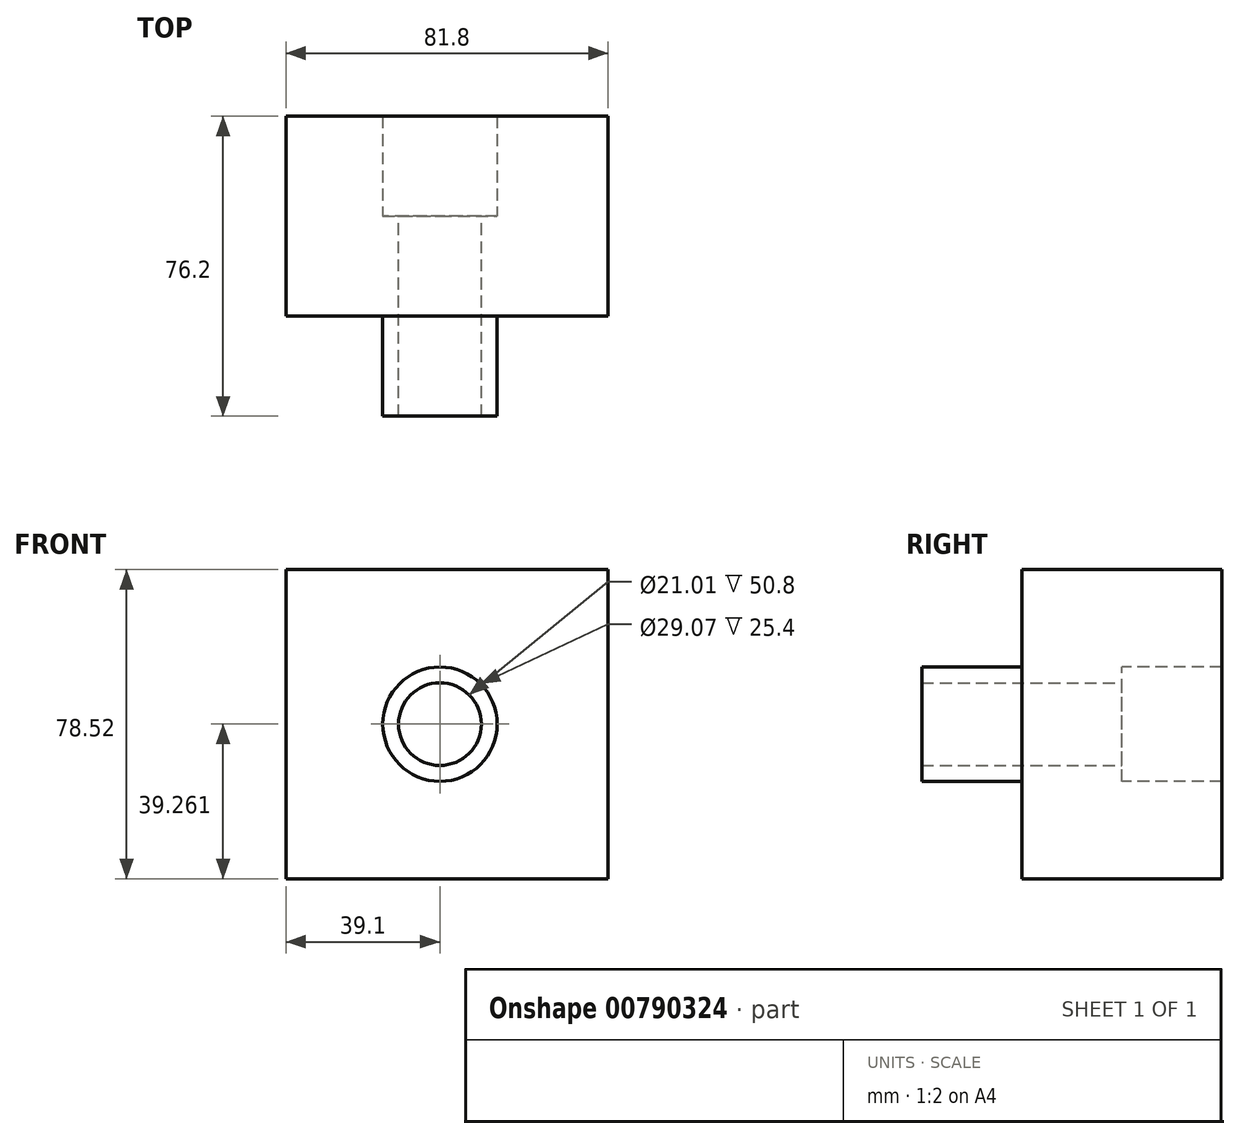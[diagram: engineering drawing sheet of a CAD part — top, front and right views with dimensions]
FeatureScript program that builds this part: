
annotation { "Feature Type Name" : "Feature", "Feature Type Description" : "" }
export const myFeature = defineFeature(function(context is Context, id is Id, definition is map)
    precondition{}
    {
        {
            var Q0;
            Q0=qCreatedBy(makeId("Front.planeOp"),FACE);
            var sketch = newSketch(context, id + "F0", { "sketchPlane" : qUnion([Q0])});
            skLineSegment(sketch, "E0.bottom", {"start": v(-39.1, 33.57) * mm, "end": v(42.7, 33.57) * mm});
            skLineSegment(sketch, "E0.top", {"start": v(-39.1, -44.95) * mm, "end": v(42.7, -44.95) * mm});
            skLineSegment(sketch, "E0.left", {"start": v(-39.1, 33.57) * mm, "end": v(-39.1, -44.95) * mm});
            skLineSegment(sketch, "E0.right", {"start": v(42.7, 33.57) * mm, "end": v(42.7, -44.95) * mm});
            skCircle(sketch, "E1", {"center": v(0, -5.69) * mm, "radius": 14.53 * mm});
            skPoint(sketch, "E1.centerSnap0", {"position": v(-39.1, -5.69) * mm});
            skCircle(sketch, "E2", {"center": v(0, -5.69) * mm, "radius": 10.5 * mm});
            skSolve(sketch);
        }
        {
            var Q0;
            Q0=makeQuery(id+"F0.imprint","IMPRINT",FACE,{"disambiguationData":[TD([[makeQuery(id+"F0.imprint","IMPRINT",EDGE,{"derivedFrom":sQuery(id+"F0.wireOp",EDGE,"E1")}),1.0]])]});
            extrude(context, id + "F1", {"entities" : qUnion([Q0]), "depth" : 50.8 * mm, "offsetDistance" : 25.4 * mm});
        }
        {
            var Q0;
            Q0=makeQuery(id+"F0.imprint","IMPRINT",FACE,{"disambiguationData":[TD([[makeQuery(id+"F0.imprint","IMPRINT",EDGE,{"derivedFrom":sQuery(id+"F0.wireOp",EDGE,"E0.right")}),-1.0]])]});
            extrude(context, id + "F2", {"entities" : qUnion([Q0]), "operationType" : NewBodyOperationType.ADD, "depth" : 25.4 * mm, "offsetDistance" : 25.4 * mm});
        }
        {
            var Q0;
            Q0=makeQuery(id+"F0.imprint","IMPRINT",FACE,{"disambiguationData":[TD([[makeQuery(id+"F0.imprint","IMPRINT",EDGE,{"derivedFrom":sQuery(id+"F0.wireOp",EDGE,"E0.right")}),-1.0]])]});
            extrude(context, id + "F3", {"entities" : qUnion([Q0]), "operationType" : NewBodyOperationType.ADD, "oppositeDirection" : true, "depth" : 25.4 * mm, "offsetDistance" : 25.4 * mm});
        }
    });
